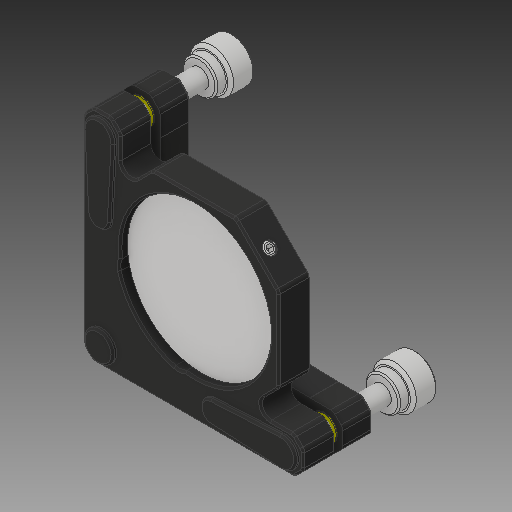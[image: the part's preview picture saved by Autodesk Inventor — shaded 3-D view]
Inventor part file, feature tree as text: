
AUTODESK INVENTOR PART (.ipt)
format: ipt  version: 2017 (Build 210142000, 142)  size: 4,390,912 bytes
history: native  units: in
note: dims shown in document units (in); Inventor stores cm internally (conversion verified against a paired STEP export)
features: other x19, mirror x1
ambient origin geometry x8: Origin, YZ Plane, XZ Plane, XY Plane, X Axis, Y Axis, Z Axis, Center Point
bodies: Solid1 (feature_tree), Solid2 (feature_tree), Solid3 (feature_tree), Solid4 (feature_tree), Solid5 (feature_tree), Solid6 (feature_tree), Solid7 (feature_tree), Solid8 (feature_tree), Solid9 (feature_tree), Solid10 (feature_tree), Solid11 (feature_tree), Solid12 (feature_tree), Solid13 (feature_tree), Solid14 (feature_tree), Solid15 (feature_tree), Solid16 (feature_tree), Solid17 (feature_tree), Solid18 (feature_tree), Solid19 (feature_tree), Solid20 (feature_tree)
feature tree (20):
  other  "6635-002-1-solid1"
  other  "6635-001A-1-solid1"
  other  "1579-006-2-solid1"
  other  "1579-006-3-solid1"
  other  "1579-004-2-solid1"
  other  "1579-004-3-solid1"
  other  "Dowel Pin_AI-1-solid1"
  other  "Dowel Pin_AI-2-solid1"
  other  "W25H042-1-solid1"
  other  "Backup of Ball 5-16-1-solid1"
  other  "Dowel Pin_AI-6-solid1"
  other  "Dowel Pin_AI-7-solid1"
  other  "Dowel Pin_AI-8-solid1"
  other  "km3-1-solid1"
  other  "km3-2-solid1"
  other  "km3-3-solid1"
  other  "Socket Set Screw Half Dog Point_AI-1-solid1"
  mirror  "mirror-1-solid1"
  other  "bushing-1-solid1"
  other  "bushing-2-solid1"
